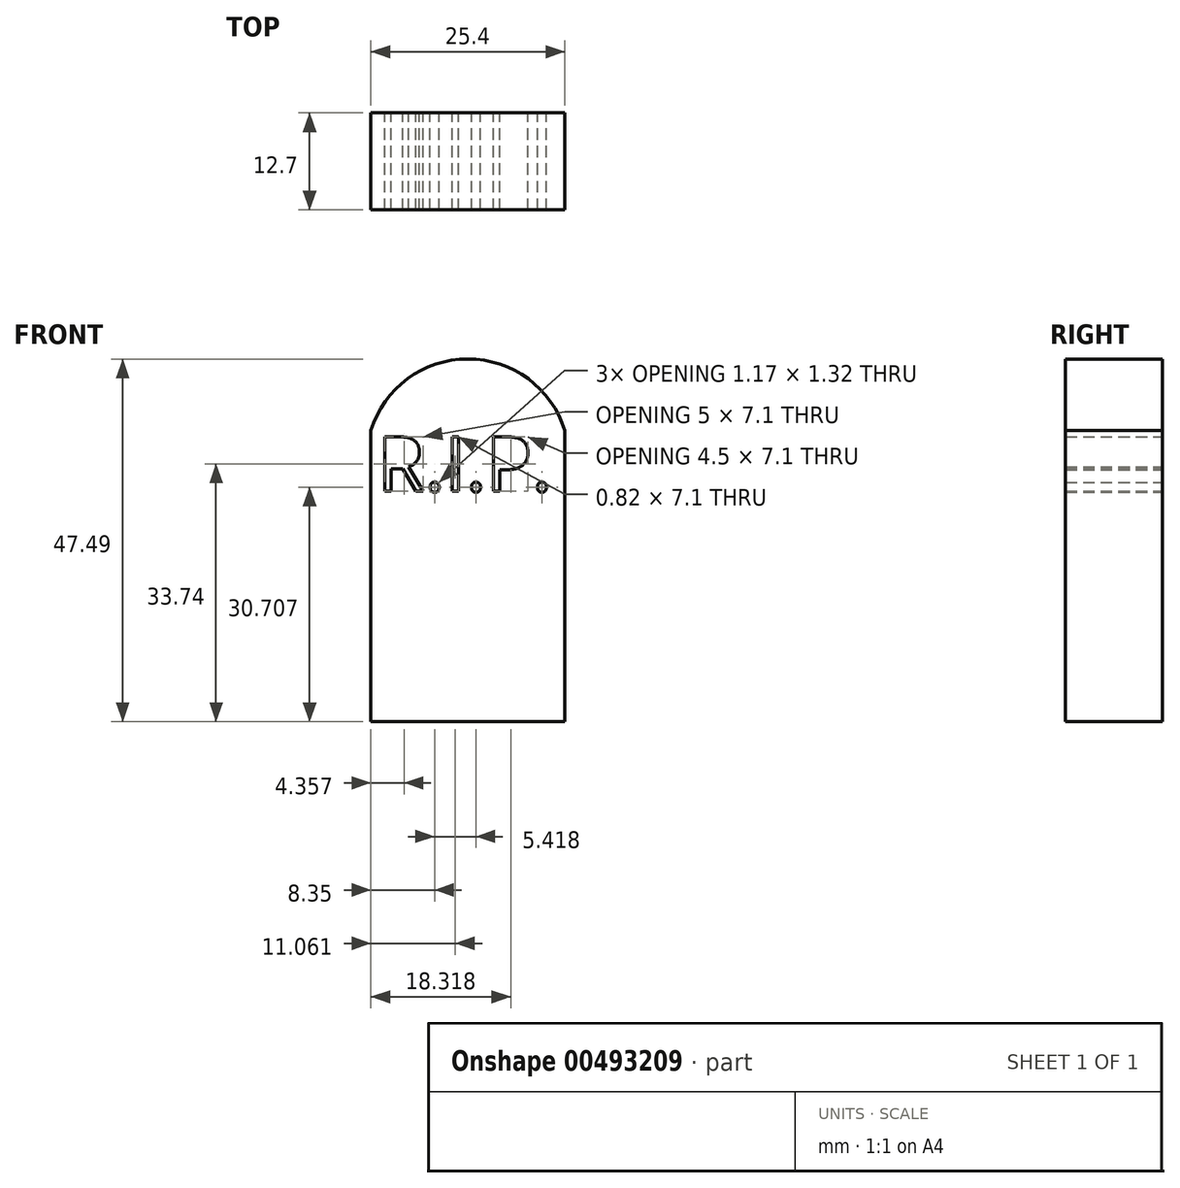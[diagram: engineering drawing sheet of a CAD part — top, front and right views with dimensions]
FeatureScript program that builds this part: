
annotation { "Feature Type Name" : "Feature", "Feature Type Description" : "" }
export const myFeature = defineFeature(function(context is Context, id is Id, definition is map)
    precondition{}
    {
        {
            var Q0;
            Q0=qCreatedBy(makeId("Front.planeOp"),FACE);
            var sketch = newSketch(context, id + "F0", { "sketchPlane" : qUnion([Q0])});
            skLineSegment(sketch, "E0", {"start": v(-12.7, 4.67) * mm, "end": v(-12.7, 42.77) * mm});
            skLineSegment(sketch, "E1.MirrorCS", {"start": v(12.7, 4.67) * mm, "end": v(12.7, 42.77) * mm});
            skLineSegment(sketch, "E2", {"start": v(-12.7, 4.67) * mm, "end": v(12.7, 4.67) * mm});
            skArc(sketch, "E3", {"start": v(12.7, 42.77) * mm, "mid": v(0, 52.16) * mm, "end": v(-12.7, 42.77) * mm});
            skText(sketch, "E4", { "text": "R.I.P.\n", "fontName": "OpenSans-Regular.ttf"});
            const initialGuessF0  = {"E4": [-0.01182, 0.03486, 1, 0, 0.00716]};
            skSetInitialGuess(sketch, initialGuessF0);
            skSolve(sketch);
        }
        {
            var Q0;
            Q0=makeQuery(id+"F0.imprint","IMPRINT",FACE,{"disambiguationData":[TD([[makeQuery(id+"F0.imprint","IMPRINT",EDGE,{"derivedFrom":sQuery(id+"F0.wireOp",EDGE,"E0")}),-1.0]])]});
            extrude(context, id + "F1", {"entities" : qUnion([Q0]), "depth" : 12.7 * mm});
        }
    });
